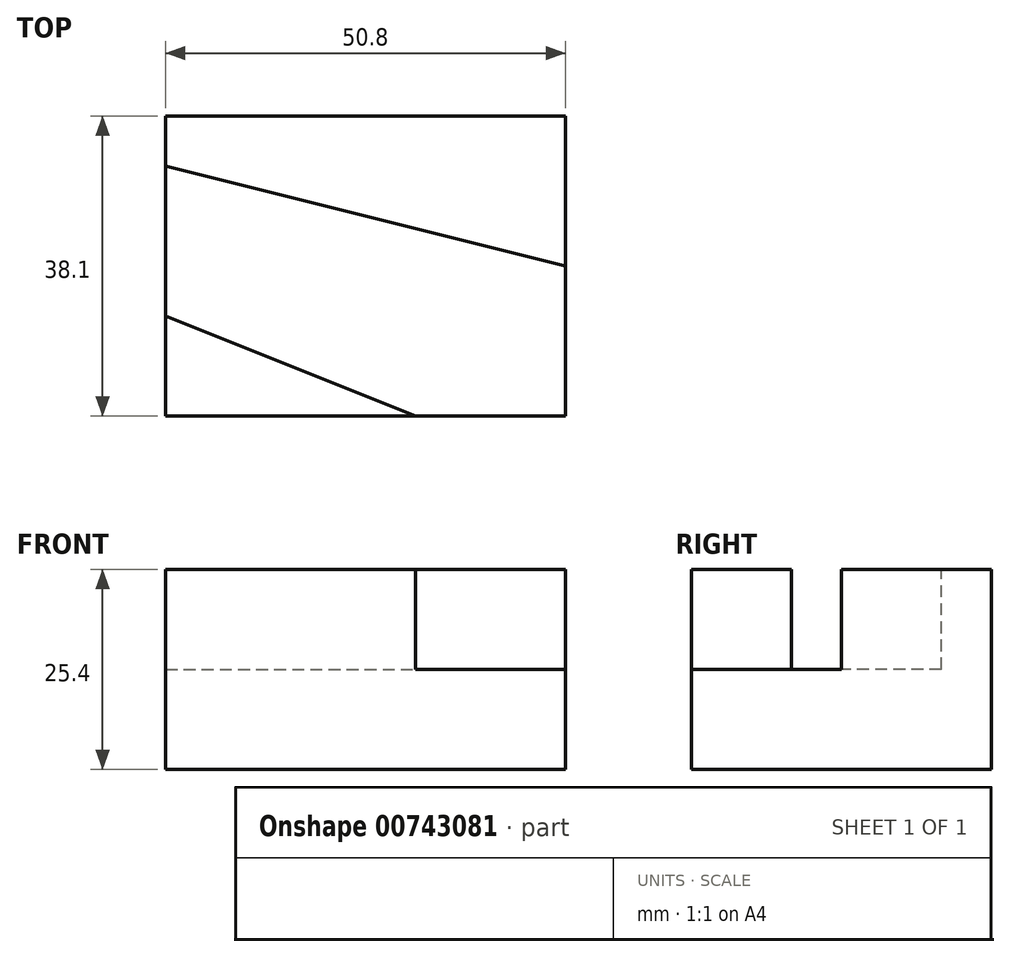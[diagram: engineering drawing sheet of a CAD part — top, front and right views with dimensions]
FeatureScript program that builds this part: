
annotation { "Feature Type Name" : "Feature", "Feature Type Description" : "" }
export const myFeature = defineFeature(function(context is Context, id is Id, definition is map)
    precondition{}
    {
        {
            var Q0;
            Q0=qCreatedBy(makeId("Top.planeOp"),FACE);
            var sketch = newSketch(context, id + "F0", { "sketchPlane" : qUnion([Q0])});
            skLineSegment(sketch, "E0", {"start": v(0, 0) * mm, "end": v(50.8, 0) * mm});
            skLineSegment(sketch, "E1", {"start": v(50.8, 0) * mm, "end": v(50.8, 38.1) * mm});
            skLineSegment(sketch, "E2", {"start": v(50.8, 38.1) * mm, "end": v(0, 38.1) * mm});
            skLineSegment(sketch, "E3", {"start": v(0, 38.1) * mm, "end": v(0, 0) * mm});
            skSolve(sketch);
        }
        {
            var Q0;
            Q0=makeQuery(id+"F0.imprint","IMPRINT",FACE,{"disambiguationData":[TD([[makeQuery(id+"F0.imprint","IMPRINT",EDGE,{"derivedFrom":sQuery(id+"F0.wireOp",EDGE,"E0")}),1.0]])]});
            extrude(context, id + "F1", {"entities" : qUnion([Q0]), "depth" : 25.4 * mm, "offsetDistance" : 25.4 * mm});
        }
        {
            var Q0;
            Q0=makeQuery(id+"F1.opExtrude","CAP_FACE",FACE,{"disambiguationData":[OSD([sQuery(id+"F0.wireOp",EDGE,"E0"),sQuery(id+"F0.wireOp",EDGE,"E1"),sQuery(id+"F0.wireOp",EDGE,"E2"),sQuery(id+"F0.wireOp",EDGE,"E3")])],"isStart":false});
            var sketch = newSketch(context, id + "F2", { "sketchPlane" : qUnion([Q0])});
            skLineSegment(sketch, "E4", {"start": v(0, 31.75) * mm, "end": v(50.8, 19.05) * mm});
            skLineSegment(sketch, "E5", {"start": v(0, 12.7) * mm, "end": v(31.75, 0) * mm});
            skSolve(sketch);
        }
        {
            var Q0;
            {var subQ4=sQuery(id+"F2.wireOp",EDGE,"E4");Q0=makeQuery(id+"F2.imprint","IMPRINT",FACE,{"disambiguationData":[TD([[makeQuery(id+"F2.imprint","IMPRINT",EDGE,{"derivedFrom":subQ4}),-1.0]])]});}
            var sketch = newSketch(context, id + "F3", { "sketchPlane" : qUnion([Q0])});
            skSolve(sketch);
        }
        {
            var Q0;
            Q0 = qSketchRegion(id + "F3", true);
            var Q1;
            {var subQ3=sQuery(id+"F2.wireOp",EDGE,"E4");Q1=makeQuery(id+"F3.imprint","IMPRINT",FACE,{"disambiguationData":[TD([[makeQuery(id+"F3.imprint","IMPRINT",EDGE,{"derivedFrom":makeQuery(id+"F2.imprint","IMPRINT",EDGE,{"derivedFrom":subQ3})}),-1.0]])]});}
            extrude(context, id + "F4", {"entities" : qUnion([Q0, Q1]), "operationType" : NewBodyOperationType.REMOVE, "oppositeDirection" : true, "depth" : 12.7 * mm, "offsetDistance" : 25.4 * mm});
        }
    });
